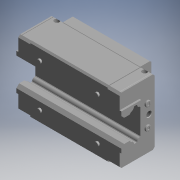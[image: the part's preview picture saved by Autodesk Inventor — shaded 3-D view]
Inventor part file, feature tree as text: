
AUTODESK INVENTOR PART (.ipt)
format: ipt  version: 2017.3 (Build 213256000, 256)  size: 420,864 bytes
history: native  units: mm (DEFAULTED — no unit token found)
features: sketch x39, extrude x22, other x21, revolve x10, hole x7, pattern_linear x1
ambient origin geometry x8: Origin, YZ Plane, XZ Plane, XY Plane, X Axis, Y Axis, Z Axis, Center Point
bodies: Solid1 (feature_tree)
feature tree (100):
  extrude  "Extrusion1"  Depth=2.0mm
  hole  "Hole1"  [1 undecoded]
  pattern_linear  "Rectangular Pattern1"  [2 undecoded]
  extrude  "Extrusion2"  [1 undecoded]
  extrude  "Extrusion3"  [1 undecoded]
  extrude  "Extrusion4"  [1 undecoded]
  extrude  "Extrusion5"  [1 undecoded]
  extrude  "Extrusion6"  [1 undecoded]
  extrude  "Extrusion7"  [1 undecoded]
  hole  "Hole2"  [1 undecoded]
  hole  "Hole3"  [1 undecoded]
  extrude  "Extrusion8"  [1 undecoded]
  extrude  "Extrusion9"  [1 undecoded]
  extrude  "Extrusion10"  [1 undecoded]
  extrude  "Extrusion11"  [1 undecoded]
  extrude  "Extrusion12"  [1 undecoded]
  revolve  "Revolution1"  [1 undecoded]
  revolve  "Revolution2"  [1 undecoded]
  revolve  "Revolution3"  [1 undecoded]
  revolve  "Revolution4"  [1 undecoded]
  extrude  "Extrusion13"  [1 undecoded]
  extrude  "Extrusion14"  [1 undecoded]
  extrude  "Extrusion15"  [1 undecoded]
  extrude  "Extrusion16"  [1 undecoded]
  extrude  "Extrusion17"  [1 undecoded]
  extrude  "Extrusion18"  [1 undecoded]
  extrude  "Extrusion19"  [1 undecoded]
  extrude  "Extrusion20"  [1 undecoded]
  extrude  "Extrusion21"  [1 undecoded]
  extrude  "Extrusion22"  [1 undecoded]
  hole  "Hole4"  [1 undecoded]
  hole  "Hole5"  [1 undecoded]
  revolve  "Revolution5"  [1 undecoded]
  revolve  "Revolution6"  [1 undecoded]
  revolve  "Revolution7"  [1 undecoded]
  revolve  "Revolution8"  [1 undecoded]
  revolve  "Revolution9"  [1 undecoded]
  hole  "Hole6"  [1 undecoded]
  revolve  "Revolution10"  [1 undecoded]
  hole  "Hole7"  [1 undecoded]
  other  "4TRACK_XY"
  other  "4TRACK_YZ"
  other  "4TRACK_ZX"
  other  "4TRACK_X"
  other  "4TRACK_Y"
  other  "4TRACK_Z"
  other  "4TRACK_Center"
  other  "niple_XY"
  other  "niple_YZ"
  other  "niple_ZX"
  other  "niple_X"
  other  "niple_Y"
  other  "niple_Z"
  other  "niple_Center"
  other  "niple2_XY"
  other  "niple2_YZ"
  other  "niple2_ZX"
  other  "niple2_X"
  other  "niple2_Y"
  other  "niple2_Z"
  other  "niple2_Center"
  sketch  "Sketch_22"  dims[d53=360.0deg]
  sketch  "Sketch2"  dims[d2=6.647mm d3=12.6765mm d4=8.0mm d5=2.0mm d6=90.0deg d7=14.4mm d8=120.0deg d9=20.0mm d11=50.0mm d12=20.0mm d14=50.0mm]
  sketch  "Sketch_7"  dims[d23=10.5mm d24=0.0mm]
  sketch  "Sketch_2"  dims[d15=11.0mm d16=0.0mm d17=3.5mm d18=0.0mm]
  sketch  "Sketch_8"  dims[d25=10.5mm d26=0.0mm]
  sketch  "Sketch_42"  dims[d82=4.917mm d83=5.5415mm d84=6.0mm d85=2.0mm d86=90.0deg d87=6.0mm d88=120.0deg]
  sketch  "Sketch_106"  dims[d102=5.2mm d103=6.0mm d104=4.0mm d105=2.0mm d106=90.0deg d107=5.2mm d108=0.0mm]
  sketch  "Sketch_107"  dims[d109=0.0mm d110=0.0mm]
  sketch  "Sketch9"  dims[d27=6.2mm d28=6.0mm d29=4.0mm d30=2.0mm d31=90.0deg d32=1.0mm d33=0.0mm]
  sketch  "Sketch10"  dims[d34=6.2mm d35=6.0mm d36=4.0mm d37=2.0mm d38=90.0deg d39=1.0mm d40=0.0mm]
  sketch  "Sketch_1"  dims[d0=80.4mm d1=0.0mm]
  sketch  "Sketch_6"  dims[d21=3.5mm d22=0.0mm]
  sketch  "Sketch_20"  dims[d51=360.0deg]
  sketch  "Sketch_21"  dims[d52=360.0deg]
  sketch  "Sketch_65"  dims[d93=360.0deg]
  sketch  "Sketch_4"  dims[d19=11.0mm d20=0.0mm]
  sketch  "Sketch_14"  dims[d45=2.0mm d46=0.0mm]
  sketch  "Sketch_15"  dims[d47=2.0mm d48=0.0mm]
  sketch  "Sketch_16"  dims[d49=109.4mm d50=0.0mm]
  sketch  "Sketch_24"  dims[d54=360.0deg]
  sketch  "Sketch_25"  dims[d55=0.75mm d56=0.0mm]
  sketch  "Sketch_26"  dims[d57=0.75mm d58=0.0mm]
  sketch  "Sketch_27"  dims[d59=0.75mm d60=0.0mm]
  sketch  "Sketch_12"  dims[d41=2.0mm d42=0.0mm]
  sketch  "Sketch_13"  dims[d43=2.0mm d44=0.0mm]
  sketch  "Sketch_45"  dims[d89=360.0deg]
  sketch  "Sketch_46"  dims[d90=360.0deg]
  sketch  "Sketch_47"  dims[d91=360.0deg]
  sketch  "Sketch_48"  dims[d92=360.0deg]
  sketch  "Sketch30"  dims[d61=0.75mm d62=0.0mm]
  sketch  "Sketch31"  dims[d63=68.0mm d64=0.0mm]
  sketch  "Sketch_34"  dims[d65=68.0mm d66=0.0mm]
  sketch  "Sketch_35"  dims[d67=47.5mm d68=0.0mm]
  sketch  "Sketch_37"  dims[d69=47.5mm d70=0.0mm]
  sketch  "Sketch_38"  dims[d73=47.5mm d74=0.0mm]
  sketch  "Sketch_94"  dims[d94=5.2mm d95=6.0mm d96=4.0mm d97=2.0mm d98=90.0deg d99=5.2mm d100=0.0mm]
  sketch  "Sketch37"  dims[d71=47.5mm d72=0.0mm]
  sketch  "Sketch_96"  dims[d101=360.0deg]
  sketch  "Sketch39"  dims[d75=4.917mm d76=5.5415mm d77=6.0mm d78=2.0mm d79=90.0deg d80=6.0mm d81=120.0deg]
note: 40 required parameter values undecoded (feature->parameter linkage not recoverable at this tier; creation-order binding heuristic only, values carry confidence <= 0.55)
